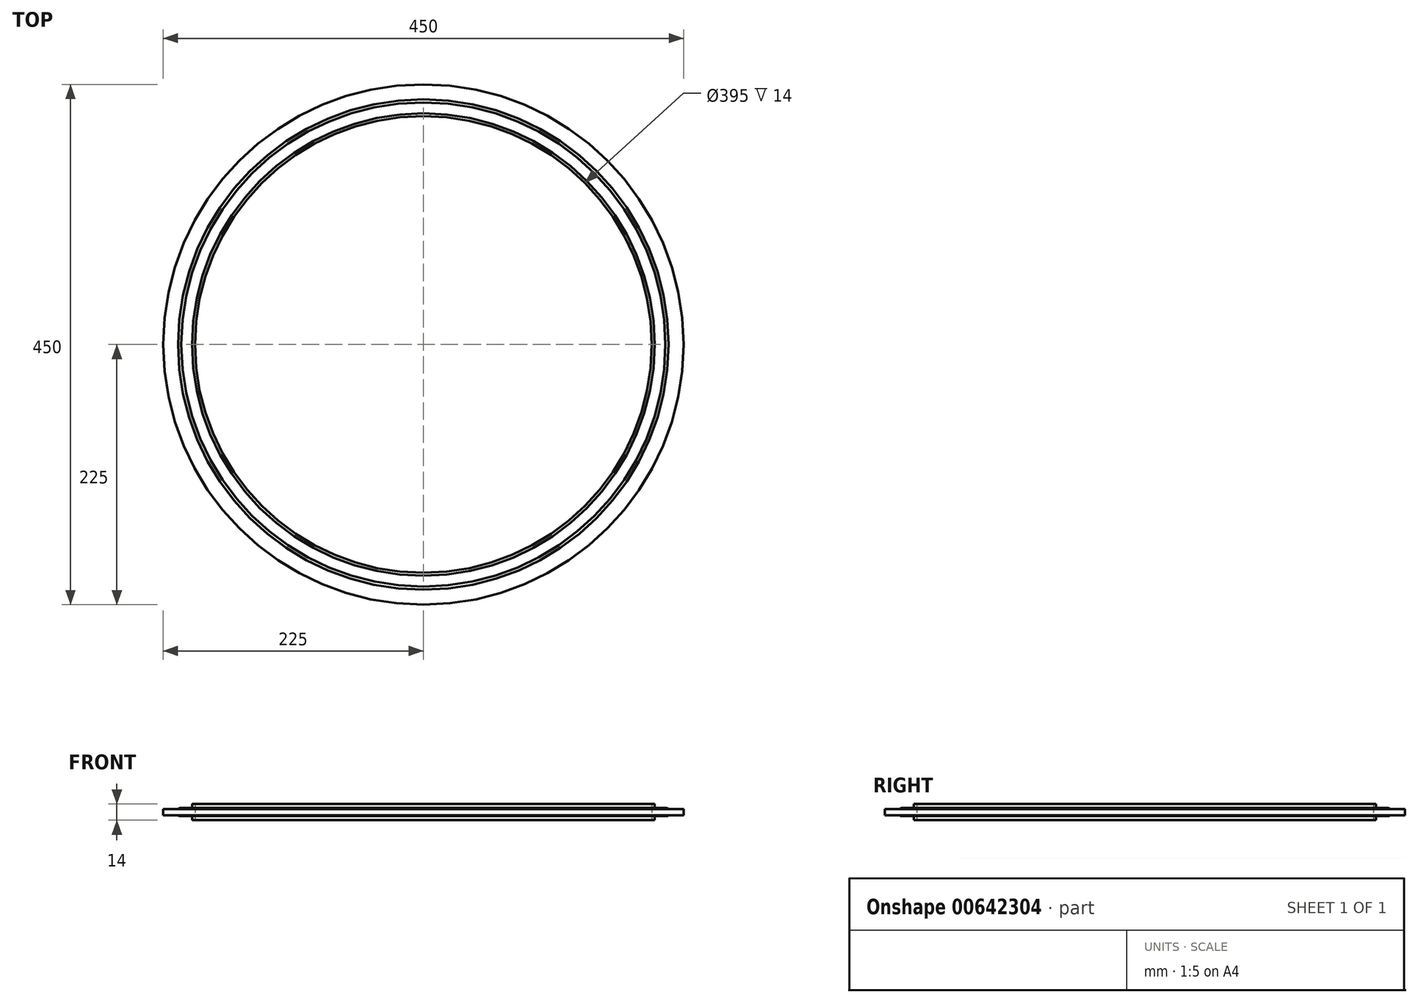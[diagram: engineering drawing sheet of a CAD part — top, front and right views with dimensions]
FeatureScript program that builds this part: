
annotation { "Feature Type Name" : "Feature", "Feature Type Description" : "" }
export const myFeature = defineFeature(function(context is Context, id is Id, definition is map)
    precondition{}
    {
        {
            var Q0;
            Q0=qCreatedBy(makeId("Front.planeOp"),FACE);
            var sketch = newSketch(context, id + "F0", { "sketchPlane" : qUnion([Q0])});
            skLineSegment(sketch, "E0", {"start": v(197.5, -7) * mm, "end": v(197.5, 7) * mm});
            skLineSegment(sketch, "E1", {"start": v(197.5, 7) * mm, "end": v(200, 7) * mm});
            skLineSegment(sketch, "E2", {"start": v(200, 7) * mm, "end": v(200, 3.45) * mm});
            skLineSegment(sketch, "E3", {"start": v(225, 2.8) * mm, "end": v(225, -2.8) * mm});
            skLineSegment(sketch, "E4", {"start": v(200, -3.45) * mm, "end": v(200, -7) * mm});
            skLineSegment(sketch, "E5", {"start": v(200, -7) * mm, "end": v(197.5, -7) * mm});
            skLineSegment(sketch, "E6", {"start": v(200, 3.45) * mm, "end": v(209.41, 3.45) * mm});
            skLineSegment(sketch, "E7", {"start": v(200, -3.45) * mm, "end": v(209.41, -3.45) * mm});
            skLineSegment(sketch, "E8", {"start": v(212.1, 2.8) * mm, "end": v(225, 2.8) * mm});
            skLineSegment(sketch, "E9", {"start": v(225, -2.8) * mm, "end": v(212.1, -2.8) * mm});
            skArc(sketch, "E10", {"start": v(209.41, -3.45) * mm, "mid": v(210.82, -3.4) * mm, "end": v(212.1, -2.8) * mm});
            skArc(sketch, "E11.trimOffspring", {"start": v(212.1, 2.8) * mm, "mid": v(210.82, 3.4) * mm, "end": v(209.41, 3.45) * mm});
            skSolve(sketch);
        }
        {
            var Q0;
            Q0=qCreatedBy(makeId("Front.planeOp"),FACE);
            var sketch = newSketch(context, id + "F1", { "sketchPlane" : qUnion([Q0])});
            skLineSegment(sketch, "E12", {"start": v(0, 0) * mm, "end": v(0, 58.33) * mm, "construction": true});
            skSolve(sketch);
        }
        {
            var Q0;
            Q0=makeQuery(id+"F0.imprint","IMPRINT",FACE,{"disambiguationData":[TD([[makeQuery(id+"F0.imprint","IMPRINT",EDGE,{"derivedFrom":sQuery(id+"F0.wireOp",EDGE,"E0")}),-1.0]])]});
            var Q1;
            Q1=sQuery(id+"F1.wireOp",EDGE,"E12");
            revolve(context, id + "F2", {"entities" : qUnion([Q0]), "axis" : qUnion([Q1]), "revolveType" : RevolveType.FULL});
        }
    });
